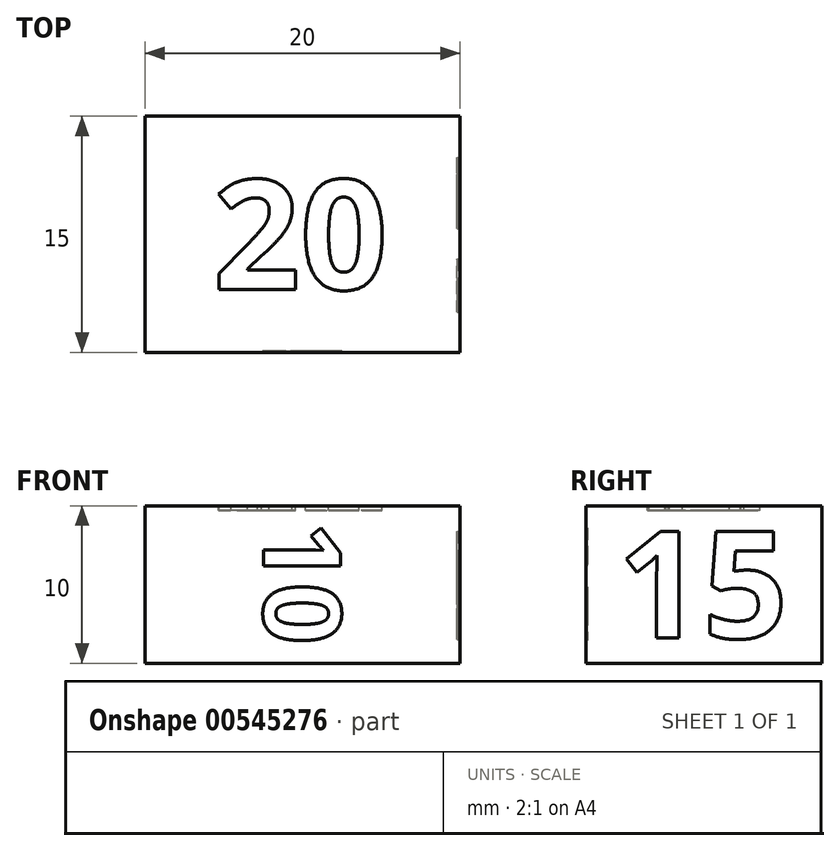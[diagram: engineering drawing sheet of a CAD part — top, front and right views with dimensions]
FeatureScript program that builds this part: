
annotation { "Feature Type Name" : "Feature", "Feature Type Description" : "" }
export const myFeature = defineFeature(function(context is Context, id is Id, definition is map)
    precondition{}
    {
        {
            var Q0;
            Q0=qCreatedBy(makeId("Top.planeOp"),FACE);
            var sketch = newSketch(context, id + "F0", { "sketchPlane" : qUnion([Q0])});
            skLineSegment(sketch, "E0.bottom", {"start": v(10, -7.5) * mm, "end": v(-10, -7.5) * mm});
            skLineSegment(sketch, "E0.top", {"start": v(10, 7.5) * mm, "end": v(-10, 7.5) * mm});
            skLineSegment(sketch, "E0.left", {"start": v(10, -7.5) * mm, "end": v(10, 7.5) * mm});
            skLineSegment(sketch, "E0.right", {"start": v(-10, -7.5) * mm, "end": v(-10, 7.5) * mm});
            skPoint(sketch, "E0.middle", {"position": v(0, 0) * mm});
            skSolve(sketch);
        }
        {
            var Q0;
            Q0 = qSketchRegion(id + "F0", true);
            extrude(context, id + "F1", {"entities" : qUnion([Q0]), "depth" : 10 * mm, "offsetDistance" : 25 * mm, "symmetric" : true});
        }
        {
            var Q0;
            Q0=makeQuery(id+"F1.opExtrude","SWEPT_FACE",FACE,{"disambiguationData":[OSD([sQuery(id+"F0.wireOp",EDGE,"E0.left")])]});
            var sketch = newSketch(context, id + "F2", { "sketchPlane" : qUnion([Q0])});
            skText(sketch, "E1", { "text": "15", "fontName": "OpenSans-Bold.ttf"});
            const initialGuessF2  = {"E1": [-0.0055, -0.0034, 1, 0, 0.00682]};
            skSetInitialGuess(sketch, initialGuessF2);
            skSolve(sketch);
        }
        {
            var Q0;
            Q0 = qSketchRegion(id + "F2", true);
            extrude(context, id + "F3", {"entities" : qUnion([Q0]), "operationType" : NewBodyOperationType.REMOVE, "oppositeDirection" : true, "depth" : 0.2 * mm, "offsetDistance" : 25 * mm});
        }
        {
            var Q0;
            Q0=makeQuery(id+"F1.opExtrude","SWEPT_FACE",FACE,{"disambiguationData":[OSD([sQuery(id+"F0.wireOp",EDGE,"E0.bottom")])]});
            var sketch = newSketch(context, id + "F4", { "sketchPlane" : qUnion([Q0])});
            skText(sketch, "E2", { "text": "10", "fontName": "OpenSans-Bold.ttf"});
            const initialGuessF4  = {"E2": [-0.00246, 0.004, 0, -1, 0.00492]};
            skSetInitialGuess(sketch, initialGuessF4);
            skSolve(sketch);
        }
        {
            var Q0;
            Q0 = qSketchRegion(id + "F4", true);
            extrude(context, id + "F5", {"entities" : qUnion([Q0]), "operationType" : NewBodyOperationType.REMOVE, "oppositeDirection" : true, "depth" : 0.1 * mm, "offsetDistance" : 25 * mm});
        }
        {
            var Q0;
            Q0=makeQuery(id+"F1.opExtrude","CAP_FACE",FACE,{"disambiguationData":[OSD([sQuery(id+"F0.wireOp",EDGE,"E0.bottom"),sQuery(id+"F0.wireOp",EDGE,"E0.top"),sQuery(id+"F0.wireOp",EDGE,"E0.left"),sQuery(id+"F0.wireOp",EDGE,"E0.right")])],"isStart":false});
            var sketch = newSketch(context, id + "F6", { "sketchPlane" : qUnion([Q0])});
            skText(sketch, "E3", { "text": "20", "fontName": "OpenSans-Bold.ttf"});
            const initialGuessF6  = {"E3": [-0.0057, -0.0035, 1, 0, 0.007]};
            skSetInitialGuess(sketch, initialGuessF6);
            skSolve(sketch);
        }
        {
            var Q0;
            Q0 = qSketchRegion(id + "F6", true);
            extrude(context, id + "F7", {"entities" : qUnion([Q0]), "operationType" : NewBodyOperationType.REMOVE, "oppositeDirection" : true, "depth" : 0.3 * mm, "offsetDistance" : 25 * mm});
        }
    });
